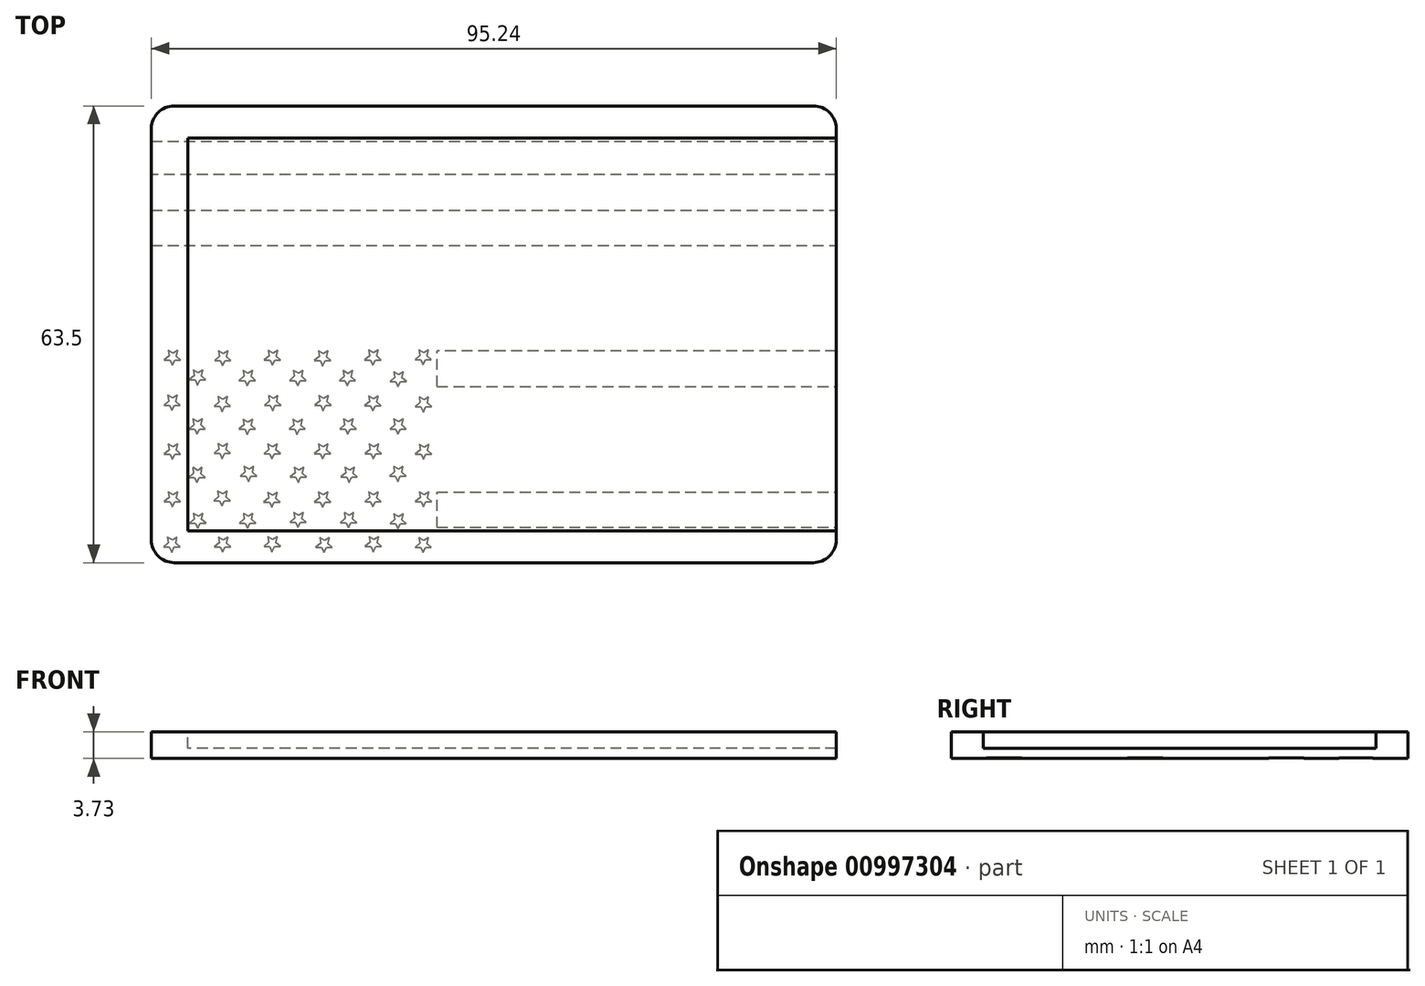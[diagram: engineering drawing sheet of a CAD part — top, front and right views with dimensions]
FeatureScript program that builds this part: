
annotation { "Feature Type Name" : "Feature", "Feature Type Description" : "" }
export const myFeature = defineFeature(function(context is Context, id is Id, definition is map)
    precondition{}
    {
        {
            var Q0;
            Q0=qCreatedBy(makeId("Top.planeOp"),FACE);
            var sketch = newSketch(context, id + "F0", { "sketchPlane" : qUnion([Q0])});
            skLineSegment(sketch, "E0.bottom", {"start": v(44.45, -31.75) * mm, "end": v(-44.45, -31.75) * mm});
            skLineSegment(sketch, "E0.top", {"start": v(44.45, 31.75) * mm, "end": v(-44.45, 31.75) * mm});
            skLineSegment(sketch, "E0.left", {"start": v(47.63, -28.57) * mm, "end": v(47.62, 28.58) * mm});
            skLineSegment(sketch, "E0.right", {"start": v(-47.63, -28.58) * mm, "end": v(-47.63, 28.57) * mm});
            skPoint(sketch, "E0.middle", {"position": v(0, 0) * mm});
            skPoint(sketch, "E1.visualSharp", {"position": v(47.62, 31.75) * mm});
            skArc(sketch, "E1.filletArc", {"start": v(47.62, 28.58) * mm, "mid": v(46.7, 30.82) * mm, "end": v(44.45, 31.75) * mm});
            skPoint(sketch, "E2.visualSharp", {"position": v(47.63, -31.75) * mm});
            skArc(sketch, "E2.filletArc", {"start": v(44.45, -31.75) * mm, "mid": v(46.7, -30.82) * mm, "end": v(47.62, -28.57) * mm});
            skPoint(sketch, "E3.visualSharp", {"position": v(-47.62, -31.75) * mm});
            skArc(sketch, "E3.filletArc", {"start": v(-47.62, -28.58) * mm, "mid": v(-46.7, -30.82) * mm, "end": v(-44.45, -31.75) * mm});
            skPoint(sketch, "E4.visualSharp", {"position": v(-47.63, 31.75) * mm});
            skArc(sketch, "E4.filletArc", {"start": v(-44.45, 31.75) * mm, "mid": v(-46.7, 30.82) * mm, "end": v(-47.63, 28.57) * mm});
            skSolve(sketch);
        }
        {
            var Q0;
            Q0=makeQuery(id+"F0.imprint","IMPRINT",FACE,{"disambiguationData":[TD([[makeQuery(id+"F0.imprint","IMPRINT",EDGE,{"derivedFrom":sQuery(id+"F0.wireOp",EDGE,"E0.bottom")}),-1.0]])]});
            extrude(context, id + "F1", {"entities" : qUnion([Q0]), "depth" : 3.73 * mm, "offsetDistance" : 25.4 * mm});
        }
        {
            var Q0;
            Q0=makeQuery(id+"F1.opExtrude","CAP_FACE",FACE,{"disambiguationData":[OSD([sQuery(id+"F0.wireOp",EDGE,"E0.bottom"),sQuery(id+"F0.wireOp",EDGE,"E0.top"),sQuery(id+"F0.wireOp",EDGE,"E0.left"),sQuery(id+"F0.wireOp",EDGE,"E0.right"),sQuery(id+"F0.wireOp",EDGE,"E1.filletArc"),sQuery(id+"F0.wireOp",EDGE,"E2.filletArc"),sQuery(id+"F0.wireOp",EDGE,"E3.filletArc"),sQuery(id+"F0.wireOp",EDGE,"E4.filletArc")])],"isStart":false});
            var sketch = newSketch(context, id + "F2", { "sketchPlane" : qUnion([Q0])});
            skLineSegment(sketch, "E5.bottom", {"start": v(47.62, 27.3) * mm, "end": v(-42.55, 27.3) * mm});
            skLineSegment(sketch, "E5.top", {"start": v(47.63, -27.3) * mm, "end": v(-42.55, -27.3) * mm});
            skLineSegment(sketch, "E5.left", {"start": v(47.62, 27.3) * mm, "end": v(47.62, -27.3) * mm});
            skLineSegment(sketch, "E5.right", {"start": v(-42.55, 27.3) * mm, "end": v(-42.55, -27.3) * mm});
            skSolve(sketch);
        }
        {
            var Q0;
            Q0=makeQuery(id+"F2.imprint","IMPRINT",FACE,{"disambiguationData":[TD([[makeQuery(id+"F2.imprint","IMPRINT",EDGE,{"derivedFrom":sQuery(id+"F2.wireOp",EDGE,"E5.bottom")}),1.0]])]});
            extrude(context, id + "F3", {"entities" : qUnion([Q0]), "operationType" : NewBodyOperationType.REMOVE, "oppositeDirection" : true, "depth" : 2.3 * mm, "offsetDistance" : 25.4 * mm});
        }
        {
            var Q0;
            Q0=makeQuery(id+"F1.opExtrude","CAP_FACE",FACE,{"disambiguationData":[OSD([sQuery(id+"F0.wireOp",EDGE,"E0.bottom"),sQuery(id+"F0.wireOp",EDGE,"E0.top"),sQuery(id+"F0.wireOp",EDGE,"E0.left"),sQuery(id+"F0.wireOp",EDGE,"E0.right"),sQuery(id+"F0.wireOp",EDGE,"E1.filletArc"),sQuery(id+"F0.wireOp",EDGE,"E2.filletArc"),sQuery(id+"F0.wireOp",EDGE,"E3.filletArc"),sQuery(id+"F0.wireOp",EDGE,"E4.filletArc")])],"isStart":true});
            var sketch = newSketch(context, id + "F4", { "sketchPlane" : qUnion([Q0])});
            skLineSegment(sketch, "E6.top", {"start": v(-8.6, 26.85) * mm, "end": v(47.63, 26.85) * mm});
            skLineSegment(sketch, "E6.left", {"start": v(-8.6, 31.75) * mm, "end": v(-8.6, 30.82) * mm});
            skLineSegment(sketch, "E7.top", {"start": v(-8.6, 21.95) * mm, "end": v(47.63, 21.95) * mm});
            skLineSegment(sketch, "E7.right", {"start": v(47.63, 26.85) * mm, "end": v(47.63, 21.95) * mm});
            skLineSegment(sketch, "E8.top", {"start": v(-8.6, 17.04) * mm, "end": v(47.63, 17.04) * mm});
            skLineSegment(sketch, "E8.right", {"start": v(47.63, 21.95) * mm, "end": v(47.63, 17.04) * mm});
            skLineSegment(sketch, "E9.right", {"start": v(47.63, 17.04) * mm, "end": v(47.63, 7.24) * mm});
            skLineSegment(sketch, "E10.bottom", {"start": v(47.63, 17.04) * mm, "end": v(-8.6, 17.04) * mm});
            skLineSegment(sketch, "E10.top", {"start": v(47.62, 12.14) * mm, "end": v(-8.16, 12.14) * mm});
            skLineSegment(sketch, "E10.left", {"start": v(47.63, 17.04) * mm, "end": v(47.63, 12.14) * mm});
            skLineSegment(sketch, "E11.left", {"start": v(47.63, 12.14) * mm, "end": v(47.63, 7.24) * mm});
            skLineSegment(sketch, "E12.bottom", {"start": v(-46.7, 7.24) * mm, "end": v(-47.63, 7.24) * mm});
            skPoint(sketch, "E13.orphan", {"position": v(47.63, 0) * mm});
            skLineSegment(sketch, "E14.bottom", {"start": v(-47.63, 7.24) * mm, "end": v(-46.7, 7.24) * mm});
            skLineSegment(sketch, "E14.right", {"start": v(47.63, 7.24) * mm, "end": v(47.63, 0) * mm});
            skLineSegment(sketch, "E15.top", {"start": v(47.62, 2.34) * mm, "end": v(-7.88, 2.34) * mm});
            skLineSegment(sketch, "E15.left", {"start": v(47.63, 2.34) * mm, "end": v(47.63, 0) * mm});
            skLineSegment(sketch, "E16.bottom", {"start": v(-47.62, 2.34) * mm, "end": v(-46.7, 2.34) * mm});
            skLineSegment(sketch, "E16.top", {"start": v(-47.63, -2.57) * mm, "end": v(47.63, -2.57) * mm});
            skLineSegment(sketch, "E16.left", {"start": v(-47.63, 2.34) * mm, "end": v(-47.63, -2.57) * mm});
            skLineSegment(sketch, "E16.right", {"start": v(47.62, 2.34) * mm, "end": v(47.62, -2.57) * mm});
            skLineSegment(sketch, "E17.bottom", {"start": v(47.63, -2.57) * mm, "end": v(-47.63, -2.57) * mm});
            skLineSegment(sketch, "E17.left", {"start": v(47.62, -2.57) * mm, "end": v(47.62, -7.47) * mm});
            skLineSegment(sketch, "E17.right", {"start": v(-47.63, -2.57) * mm, "end": v(-47.63, -7.47) * mm});
            skLineSegment(sketch, "E18.bottom", {"start": v(47.62, -7.47) * mm, "end": v(-47.63, -7.47) * mm});
            skPoint(sketch, "E19.orphan", {"position": v(-7.88, 0) * mm});
            skLineSegment(sketch, "E20.bottom", {"start": v(-47.63, -7.47) * mm, "end": v(47.62, -7.47) * mm});
            skLineSegment(sketch, "E20.top", {"start": v(-47.63, -12.37) * mm, "end": v(47.62, -12.37) * mm});
            skLineSegment(sketch, "E20.left", {"start": v(-47.63, -7.47) * mm, "end": v(-47.63, -12.37) * mm});
            skLineSegment(sketch, "E20.right", {"start": v(47.62, -7.47) * mm, "end": v(47.62, -12.37) * mm});
            skLineSegment(sketch, "E21.top", {"start": v(-47.63, -17.27) * mm, "end": v(47.62, -17.27) * mm});
            skLineSegment(sketch, "E21.left", {"start": v(-47.63, -12.37) * mm, "end": v(-47.63, -17.27) * mm});
            skLineSegment(sketch, "E21.right", {"start": v(47.62, -12.37) * mm, "end": v(47.62, -17.27) * mm});
            skLineSegment(sketch, "E22.bottom", {"start": v(47.62, -17.27) * mm, "end": v(-47.63, -17.27) * mm});
            skLineSegment(sketch, "E22.top", {"start": v(47.62, -22.17) * mm, "end": v(-47.63, -22.17) * mm});
            skLineSegment(sketch, "E22.left", {"start": v(47.62, -17.27) * mm, "end": v(47.62, -22.17) * mm});
            skLineSegment(sketch, "E22.right", {"start": v(-47.63, -17.27) * mm, "end": v(-47.63, -22.17) * mm});
            skLineSegment(sketch, "E23", {"start": v(-47.63, -26.85) * mm, "end": v(47.62, -26.85) * mm});
            skLineSegment(sketch, "E24.trimOffspring", {"start": v(-8.05, 7.24) * mm, "end": v(47.63, 7.24) * mm});
            skPoint(sketch, "E25.left.start.orphan", {"position": v(-46.7, 30.82) * mm});
            skLineSegment(sketch, "E26.bottom", {"start": v(-8.6, 30.82) * mm, "end": v(-7.88, 30.82) * mm});
            skLineSegment(sketch, "E26.right", {"start": v(-7.88, 30.82) * mm, "end": v(-7.88, 2.34) * mm});
            skLineSegment(sketch, "E27.trimOffspring", {"start": v(-7.88, 2.34) * mm, "end": v(47.62, 2.34) * mm});
            skPoint(sketch, "E25.right.start.orphan", {"position": v(-8.6, 30.82) * mm});
            skLineSegment(sketch, "E28", {"start": v(-45.92, 29.59) * mm, "end": v(-45.14, 29.59) * mm});
            skLineSegment(sketch, "E29", {"start": v(-45.14, 29.59) * mm, "end": v(-44.8, 30.3) * mm});
            skLineSegment(sketch, "E30", {"start": v(-44.8, 30.3) * mm, "end": v(-44.44, 29.59) * mm});
            skLineSegment(sketch, "E31", {"start": v(-44.44, 29.59) * mm, "end": v(-43.65, 29.59) * mm});
            skLineSegment(sketch, "E32", {"start": v(-43.65, 29.59) * mm, "end": v(-44.23, 29.06) * mm});
            skLineSegment(sketch, "E33", {"start": v(-44.23, 29.06) * mm, "end": v(-44.06, 28.23) * mm});
            skLineSegment(sketch, "E34", {"start": v(-44.06, 28.23) * mm, "end": v(-44.67, 28.61) * mm});
            skLineSegment(sketch, "E35", {"start": v(-44.67, 28.61) * mm, "end": v(-45.38, 28.23) * mm});
            skLineSegment(sketch, "E36", {"start": v(-45.38, 28.23) * mm, "end": v(-45.26, 29.01) * mm});
            skLineSegment(sketch, "E37", {"start": v(-45.26, 29.01) * mm, "end": v(-45.92, 29.59) * mm});
            skLineSegment(sketch, "E38", {"start": v(-38.84, 29.57) * mm, "end": v(-38.05, 29.57) * mm});
            skLineSegment(sketch, "E39", {"start": v(-38.05, 29.57) * mm, "end": v(-37.71, 30.28) * mm});
            skLineSegment(sketch, "E40", {"start": v(-37.71, 30.28) * mm, "end": v(-37.36, 29.57) * mm});
            skLineSegment(sketch, "E41", {"start": v(-37.36, 29.57) * mm, "end": v(-36.57, 29.57) * mm});
            skLineSegment(sketch, "E42", {"start": v(-36.57, 29.57) * mm, "end": v(-37.14, 29.04) * mm});
            skLineSegment(sketch, "E43", {"start": v(-37.14, 29.04) * mm, "end": v(-36.97, 28.2) * mm});
            skLineSegment(sketch, "E44", {"start": v(-36.97, 28.2) * mm, "end": v(-37.59, 28.6) * mm});
            skLineSegment(sketch, "E45", {"start": v(-37.59, 28.6) * mm, "end": v(-38.3, 28.2) * mm});
            skLineSegment(sketch, "E46", {"start": v(-38.3, 28.2) * mm, "end": v(-38.18, 29) * mm});
            skLineSegment(sketch, "E47", {"start": v(-38.18, 29) * mm, "end": v(-38.84, 29.57) * mm});
            skLineSegment(sketch, "E48", {"start": v(-21.49, 6.44) * mm, "end": v(-20.7, 6.44) * mm});
            skLineSegment(sketch, "E49", {"start": v(-20.7, 6.44) * mm, "end": v(-20.36, 7.15) * mm});
            skLineSegment(sketch, "E50", {"start": v(-20.36, 7.15) * mm, "end": v(-20, 6.44) * mm});
            skLineSegment(sketch, "E51", {"start": v(-20, 6.44) * mm, "end": v(-19.22, 6.44) * mm});
            skLineSegment(sketch, "E52", {"start": v(-19.22, 6.44) * mm, "end": v(-19.8, 5.91) * mm});
            skLineSegment(sketch, "E53", {"start": v(-19.8, 5.91) * mm, "end": v(-19.62, 5.08) * mm});
            skLineSegment(sketch, "E54", {"start": v(-19.62, 5.08) * mm, "end": v(-20.23, 5.47) * mm});
            skLineSegment(sketch, "E55", {"start": v(-20.23, 5.47) * mm, "end": v(-20.94, 5.08) * mm});
            skLineSegment(sketch, "E56", {"start": v(-20.94, 5.08) * mm, "end": v(-20.82, 5.86) * mm});
            skLineSegment(sketch, "E57", {"start": v(-20.82, 5.86) * mm, "end": v(-21.49, 6.44) * mm});
            skLineSegment(sketch, "E58", {"start": v(-17.94, 3.57) * mm, "end": v(-17.16, 3.57) * mm});
            skLineSegment(sketch, "E59", {"start": v(-17.16, 3.57) * mm, "end": v(-16.82, 4.29) * mm});
            skLineSegment(sketch, "E60", {"start": v(-16.82, 4.29) * mm, "end": v(-16.46, 3.57) * mm});
            skLineSegment(sketch, "E61", {"start": v(-16.46, 3.57) * mm, "end": v(-15.67, 3.57) * mm});
            skLineSegment(sketch, "E62", {"start": v(-15.67, 3.57) * mm, "end": v(-16.25, 3.05) * mm});
            skLineSegment(sketch, "E63", {"start": v(-16.25, 3.05) * mm, "end": v(-16.07, 2.21) * mm});
            skLineSegment(sketch, "E64", {"start": v(-16.07, 2.21) * mm, "end": v(-16.69, 2.6) * mm});
            skLineSegment(sketch, "E65", {"start": v(-16.69, 2.6) * mm, "end": v(-17.4, 2.21) * mm});
            skLineSegment(sketch, "E66", {"start": v(-17.4, 2.21) * mm, "end": v(-17.28, 3) * mm});
            skLineSegment(sketch, "E67", {"start": v(-17.28, 3) * mm, "end": v(-17.94, 3.57) * mm});
            skLineSegment(sketch, "E68", {"start": v(-14.43, 6.57) * mm, "end": v(-13.65, 6.57) * mm});
            skLineSegment(sketch, "E69", {"start": v(-13.65, 6.57) * mm, "end": v(-13.3, 7.29) * mm});
            skLineSegment(sketch, "E70", {"start": v(-13.3, 7.29) * mm, "end": v(-12.95, 6.57) * mm});
            skLineSegment(sketch, "E71", {"start": v(-12.95, 6.57) * mm, "end": v(-12.16, 6.57) * mm});
            skLineSegment(sketch, "E72", {"start": v(-12.16, 6.57) * mm, "end": v(-12.74, 6.05) * mm});
            skLineSegment(sketch, "E73", {"start": v(-12.74, 6.05) * mm, "end": v(-12.56, 5.21) * mm});
            skLineSegment(sketch, "E74", {"start": v(-12.56, 5.21) * mm, "end": v(-13.18, 5.6) * mm});
            skLineSegment(sketch, "E75", {"start": v(-13.18, 5.6) * mm, "end": v(-13.9, 5.21) * mm});
            skLineSegment(sketch, "E76", {"start": v(-13.9, 5.21) * mm, "end": v(-13.77, 6) * mm});
            skLineSegment(sketch, "E77", {"start": v(-13.77, 6) * mm, "end": v(-14.43, 6.57) * mm});
            skLineSegment(sketch, "E78", {"start": v(-10.94, 3.53) * mm, "end": v(-10.16, 3.53) * mm});
            skLineSegment(sketch, "E79", {"start": v(-10.16, 3.53) * mm, "end": v(-9.82, 4.25) * mm});
            skLineSegment(sketch, "E80", {"start": v(-9.82, 4.25) * mm, "end": v(-9.46, 3.53) * mm});
            skLineSegment(sketch, "E81", {"start": v(-9.46, 3.53) * mm, "end": v(-8.67, 3.53) * mm});
            skLineSegment(sketch, "E82", {"start": v(-8.67, 3.53) * mm, "end": v(-9.25, 3) * mm});
            skLineSegment(sketch, "E83", {"start": v(-9.25, 3) * mm, "end": v(-9.08, 2.17) * mm});
            skLineSegment(sketch, "E84", {"start": v(-9.08, 2.17) * mm, "end": v(-9.7, 2.56) * mm});
            skLineSegment(sketch, "E85", {"start": v(-9.7, 2.56) * mm, "end": v(-10.4, 2.17) * mm});
            skLineSegment(sketch, "E86", {"start": v(-10.4, 2.17) * mm, "end": v(-10.28, 2.96) * mm});
            skLineSegment(sketch, "E87", {"start": v(-10.28, 2.96) * mm, "end": v(-10.94, 3.53) * mm});
            skLineSegment(sketch, "E88", {"start": v(-10.92, 10.08) * mm, "end": v(-10.14, 10.08) * mm});
            skLineSegment(sketch, "E89", {"start": v(-10.14, 10.08) * mm, "end": v(-9.8, 10.8) * mm});
            skLineSegment(sketch, "E90", {"start": v(-9.8, 10.8) * mm, "end": v(-9.44, 10.08) * mm});
            skLineSegment(sketch, "E91", {"start": v(-9.44, 10.08) * mm, "end": v(-8.65, 10.08) * mm});
            skLineSegment(sketch, "E92", {"start": v(-8.65, 10.08) * mm, "end": v(-9.23, 9.56) * mm});
            skLineSegment(sketch, "E93", {"start": v(-9.23, 9.56) * mm, "end": v(-9.06, 8.72) * mm});
            skLineSegment(sketch, "E94", {"start": v(-9.06, 8.72) * mm, "end": v(-9.67, 9.1) * mm});
            skLineSegment(sketch, "E95", {"start": v(-9.67, 9.1) * mm, "end": v(-10.38, 8.72) * mm});
            skLineSegment(sketch, "E96", {"start": v(-10.38, 8.72) * mm, "end": v(-10.26, 9.5) * mm});
            skLineSegment(sketch, "E97", {"start": v(-10.26, 9.5) * mm, "end": v(-10.92, 10.08) * mm});
            skLineSegment(sketch, "E98", {"start": v(-17.96, 9.95) * mm, "end": v(-17.17, 9.95) * mm});
            skLineSegment(sketch, "E99", {"start": v(-17.17, 9.95) * mm, "end": v(-16.83, 10.66) * mm});
            skLineSegment(sketch, "E100", {"start": v(-16.83, 10.66) * mm, "end": v(-16.48, 9.95) * mm});
            skLineSegment(sketch, "E101", {"start": v(-16.48, 9.95) * mm, "end": v(-15.69, 9.95) * mm});
            skLineSegment(sketch, "E102", {"start": v(-15.69, 9.95) * mm, "end": v(-16.26, 9.42) * mm});
            skLineSegment(sketch, "E103", {"start": v(-16.26, 9.42) * mm, "end": v(-16.1, 8.59) * mm});
            skLineSegment(sketch, "E104", {"start": v(-16.1, 8.59) * mm, "end": v(-16.7, 8.97) * mm});
            skLineSegment(sketch, "E105", {"start": v(-16.7, 8.97) * mm, "end": v(-17.42, 8.59) * mm});
            skLineSegment(sketch, "E106", {"start": v(-17.42, 8.59) * mm, "end": v(-17.3, 9.37) * mm});
            skLineSegment(sketch, "E107", {"start": v(-17.3, 9.37) * mm, "end": v(-17.96, 9.95) * mm});
            skLineSegment(sketch, "E108", {"start": v(-24.93, 3.67) * mm, "end": v(-24.15, 3.67) * mm});
            skLineSegment(sketch, "E109", {"start": v(-24.15, 3.67) * mm, "end": v(-23.81, 4.38) * mm});
            skLineSegment(sketch, "E110", {"start": v(-23.81, 4.38) * mm, "end": v(-23.45, 3.67) * mm});
            skLineSegment(sketch, "E111", {"start": v(-23.45, 3.67) * mm, "end": v(-22.66, 3.67) * mm});
            skLineSegment(sketch, "E112", {"start": v(-22.66, 3.67) * mm, "end": v(-23.24, 3.14) * mm});
            skLineSegment(sketch, "E113", {"start": v(-23.24, 3.14) * mm, "end": v(-23.07, 2.3) * mm});
            skLineSegment(sketch, "E114", {"start": v(-23.07, 2.3) * mm, "end": v(-23.68, 2.7) * mm});
            skLineSegment(sketch, "E115", {"start": v(-23.68, 2.7) * mm, "end": v(-24.4, 2.3) * mm});
            skLineSegment(sketch, "E116", {"start": v(-24.4, 2.3) * mm, "end": v(-24.27, 3.1) * mm});
            skLineSegment(sketch, "E117", {"start": v(-24.27, 3.1) * mm, "end": v(-24.93, 3.67) * mm});
            skLineSegment(sketch, "E118", {"start": v(-42.3, 26.26) * mm, "end": v(-41.52, 26.26) * mm});
            skLineSegment(sketch, "E119", {"start": v(-41.52, 26.26) * mm, "end": v(-41.18, 26.97) * mm});
            skLineSegment(sketch, "E120", {"start": v(-41.18, 26.97) * mm, "end": v(-40.82, 26.26) * mm});
            skLineSegment(sketch, "E121", {"start": v(-40.82, 26.26) * mm, "end": v(-40.04, 26.26) * mm});
            skLineSegment(sketch, "E122", {"start": v(-40.04, 26.26) * mm, "end": v(-40.61, 25.73) * mm});
            skLineSegment(sketch, "E123", {"start": v(-40.61, 25.73) * mm, "end": v(-40.44, 24.9) * mm});
            skLineSegment(sketch, "E124", {"start": v(-40.44, 24.9) * mm, "end": v(-41.05, 25.28) * mm});
            skLineSegment(sketch, "E125", {"start": v(-41.05, 25.28) * mm, "end": v(-41.76, 24.9) * mm});
            skLineSegment(sketch, "E126", {"start": v(-41.76, 24.9) * mm, "end": v(-41.64, 25.68) * mm});
            skLineSegment(sketch, "E127", {"start": v(-41.64, 25.68) * mm, "end": v(-42.3, 26.26) * mm});
            skLineSegment(sketch, "E128", {"start": v(-45.83, 23.27) * mm, "end": v(-45.05, 23.27) * mm});
            skLineSegment(sketch, "E129", {"start": v(-45.05, 23.27) * mm, "end": v(-44.7, 23.99) * mm});
            skLineSegment(sketch, "E130", {"start": v(-44.7, 23.99) * mm, "end": v(-44.35, 23.27) * mm});
            skLineSegment(sketch, "E131", {"start": v(-44.35, 23.27) * mm, "end": v(-43.56, 23.27) * mm});
            skLineSegment(sketch, "E132", {"start": v(-43.56, 23.27) * mm, "end": v(-44.14, 22.75) * mm});
            skLineSegment(sketch, "E133", {"start": v(-44.14, 22.75) * mm, "end": v(-43.97, 21.91) * mm});
            skLineSegment(sketch, "E134", {"start": v(-43.97, 21.91) * mm, "end": v(-44.58, 22.3) * mm});
            skLineSegment(sketch, "E135", {"start": v(-44.58, 22.3) * mm, "end": v(-45.3, 21.91) * mm});
            skLineSegment(sketch, "E136", {"start": v(-45.3, 21.91) * mm, "end": v(-45.17, 22.7) * mm});
            skLineSegment(sketch, "E137", {"start": v(-45.17, 22.7) * mm, "end": v(-45.83, 23.27) * mm});
            skLineSegment(sketch, "E138", {"start": v(-38.93, 23.16) * mm, "end": v(-38.15, 23.16) * mm});
            skLineSegment(sketch, "E139", {"start": v(-38.15, 23.16) * mm, "end": v(-37.8, 23.87) * mm});
            skLineSegment(sketch, "E140", {"start": v(-37.8, 23.87) * mm, "end": v(-37.45, 23.16) * mm});
            skLineSegment(sketch, "E141", {"start": v(-37.45, 23.16) * mm, "end": v(-36.66, 23.16) * mm});
            skLineSegment(sketch, "E142", {"start": v(-36.66, 23.16) * mm, "end": v(-37.24, 22.63) * mm});
            skLineSegment(sketch, "E143", {"start": v(-37.24, 22.63) * mm, "end": v(-37.07, 21.8) * mm});
            skLineSegment(sketch, "E144", {"start": v(-37.07, 21.8) * mm, "end": v(-37.68, 22.18) * mm});
            skLineSegment(sketch, "E145", {"start": v(-37.68, 22.18) * mm, "end": v(-38.4, 21.8) * mm});
            skLineSegment(sketch, "E146", {"start": v(-38.4, 21.8) * mm, "end": v(-38.27, 22.58) * mm});
            skLineSegment(sketch, "E147", {"start": v(-38.27, 22.58) * mm, "end": v(-38.93, 23.16) * mm});
            skLineSegment(sketch, "E148", {"start": v(-35.37, 26.26) * mm, "end": v(-34.58, 26.26) * mm});
            skLineSegment(sketch, "E149", {"start": v(-34.58, 26.26) * mm, "end": v(-34.24, 26.97) * mm});
            skLineSegment(sketch, "E150", {"start": v(-34.24, 26.97) * mm, "end": v(-33.89, 26.26) * mm});
            skLineSegment(sketch, "E151", {"start": v(-33.89, 26.26) * mm, "end": v(-33.1, 26.26) * mm});
            skLineSegment(sketch, "E152", {"start": v(-33.1, 26.26) * mm, "end": v(-33.67, 25.73) * mm});
            skLineSegment(sketch, "E153", {"start": v(-33.67, 25.73) * mm, "end": v(-33.5, 24.9) * mm});
            skLineSegment(sketch, "E154", {"start": v(-33.5, 24.9) * mm, "end": v(-34.12, 25.28) * mm});
            skLineSegment(sketch, "E155", {"start": v(-34.12, 25.28) * mm, "end": v(-34.83, 24.9) * mm});
            skLineSegment(sketch, "E156", {"start": v(-34.83, 24.9) * mm, "end": v(-34.7, 25.68) * mm});
            skLineSegment(sketch, "E157", {"start": v(-34.7, 25.68) * mm, "end": v(-35.37, 26.26) * mm});
            skLineSegment(sketch, "E158", {"start": v(-31.96, 29.51) * mm, "end": v(-31.17, 29.51) * mm});
            skLineSegment(sketch, "E159", {"start": v(-31.17, 29.51) * mm, "end": v(-30.83, 30.23) * mm});
            skLineSegment(sketch, "E160", {"start": v(-30.83, 30.23) * mm, "end": v(-30.48, 29.51) * mm});
            skLineSegment(sketch, "E161", {"start": v(-30.48, 29.51) * mm, "end": v(-29.69, 29.51) * mm});
            skLineSegment(sketch, "E162", {"start": v(-29.69, 29.51) * mm, "end": v(-30.26, 28.99) * mm});
            skLineSegment(sketch, "E163", {"start": v(-30.26, 28.99) * mm, "end": v(-30.1, 28.15) * mm});
            skLineSegment(sketch, "E164", {"start": v(-30.1, 28.15) * mm, "end": v(-30.7, 28.54) * mm});
            skLineSegment(sketch, "E165", {"start": v(-30.7, 28.54) * mm, "end": v(-31.42, 28.15) * mm});
            skLineSegment(sketch, "E166", {"start": v(-31.42, 28.15) * mm, "end": v(-31.3, 28.94) * mm});
            skLineSegment(sketch, "E167", {"start": v(-31.3, 28.94) * mm, "end": v(-31.96, 29.51) * mm});
            skLineSegment(sketch, "E168", {"start": v(-28.35, 26.14) * mm, "end": v(-27.57, 26.14) * mm});
            skLineSegment(sketch, "E169", {"start": v(-27.57, 26.14) * mm, "end": v(-27.23, 26.86) * mm});
            skLineSegment(sketch, "E170", {"start": v(-27.23, 26.86) * mm, "end": v(-26.87, 26.14) * mm});
            skLineSegment(sketch, "E171", {"start": v(-26.87, 26.14) * mm, "end": v(-26.08, 26.14) * mm});
            skLineSegment(sketch, "E172", {"start": v(-26.08, 26.14) * mm, "end": v(-26.66, 25.62) * mm});
            skLineSegment(sketch, "E173", {"start": v(-26.66, 25.62) * mm, "end": v(-26.49, 24.78) * mm});
            skLineSegment(sketch, "E174", {"start": v(-26.49, 24.78) * mm, "end": v(-27.1, 25.17) * mm});
            skLineSegment(sketch, "E175", {"start": v(-27.1, 25.17) * mm, "end": v(-27.81, 24.78) * mm});
            skLineSegment(sketch, "E176", {"start": v(-27.81, 24.78) * mm, "end": v(-27.7, 25.56) * mm});
            skLineSegment(sketch, "E177", {"start": v(-27.7, 25.56) * mm, "end": v(-28.35, 26.14) * mm});
            skLineSegment(sketch, "E178", {"start": v(-24.75, 29.63) * mm, "end": v(-23.97, 29.63) * mm});
            skLineSegment(sketch, "E179", {"start": v(-23.97, 29.63) * mm, "end": v(-23.63, 30.34) * mm});
            skLineSegment(sketch, "E180", {"start": v(-23.63, 30.34) * mm, "end": v(-23.27, 29.63) * mm});
            skLineSegment(sketch, "E181", {"start": v(-23.27, 29.63) * mm, "end": v(-22.48, 29.63) * mm});
            skLineSegment(sketch, "E182", {"start": v(-22.48, 29.63) * mm, "end": v(-23.05, 29.1) * mm});
            skLineSegment(sketch, "E183", {"start": v(-23.05, 29.1) * mm, "end": v(-22.88, 28.27) * mm});
            skLineSegment(sketch, "E184", {"start": v(-22.88, 28.27) * mm, "end": v(-23.5, 28.66) * mm});
            skLineSegment(sketch, "E185", {"start": v(-23.5, 28.66) * mm, "end": v(-24.2, 28.27) * mm});
            skLineSegment(sketch, "E186", {"start": v(-24.2, 28.27) * mm, "end": v(-24.09, 29.05) * mm});
            skLineSegment(sketch, "E187", {"start": v(-24.09, 29.05) * mm, "end": v(-24.75, 29.63) * mm});
            skLineSegment(sketch, "E188", {"start": v(-21.34, 26.18) * mm, "end": v(-20.55, 26.18) * mm});
            skLineSegment(sketch, "E189", {"start": v(-20.55, 26.18) * mm, "end": v(-20.21, 26.9) * mm});
            skLineSegment(sketch, "E190", {"start": v(-20.21, 26.9) * mm, "end": v(-19.86, 26.18) * mm});
            skLineSegment(sketch, "E191", {"start": v(-19.86, 26.18) * mm, "end": v(-19.07, 26.18) * mm});
            skLineSegment(sketch, "E192", {"start": v(-19.07, 26.18) * mm, "end": v(-19.64, 25.66) * mm});
            skLineSegment(sketch, "E193", {"start": v(-19.64, 25.66) * mm, "end": v(-19.47, 24.82) * mm});
            skLineSegment(sketch, "E194", {"start": v(-19.47, 24.82) * mm, "end": v(-20.09, 25.2) * mm});
            skLineSegment(sketch, "E195", {"start": v(-20.09, 25.2) * mm, "end": v(-20.8, 24.82) * mm});
            skLineSegment(sketch, "E196", {"start": v(-20.8, 24.82) * mm, "end": v(-20.68, 25.6) * mm});
            skLineSegment(sketch, "E197", {"start": v(-20.68, 25.6) * mm, "end": v(-21.34, 26.18) * mm});
            skLineSegment(sketch, "E198", {"start": v(-17.89, 29.51) * mm, "end": v(-17.1, 29.51) * mm});
            skLineSegment(sketch, "E199", {"start": v(-17.1, 29.51) * mm, "end": v(-16.77, 30.23) * mm});
            skLineSegment(sketch, "E200", {"start": v(-16.77, 30.23) * mm, "end": v(-16.4, 29.51) * mm});
            skLineSegment(sketch, "E201", {"start": v(-16.4, 29.51) * mm, "end": v(-15.62, 29.51) * mm});
            skLineSegment(sketch, "E202", {"start": v(-15.62, 29.51) * mm, "end": v(-16.2, 28.99) * mm});
            skLineSegment(sketch, "E203", {"start": v(-16.2, 28.99) * mm, "end": v(-16.02, 28.15) * mm});
            skLineSegment(sketch, "E204", {"start": v(-16.02, 28.15) * mm, "end": v(-16.64, 28.54) * mm});
            skLineSegment(sketch, "E205", {"start": v(-16.64, 28.54) * mm, "end": v(-17.35, 28.15) * mm});
            skLineSegment(sketch, "E206", {"start": v(-17.35, 28.15) * mm, "end": v(-17.23, 28.94) * mm});
            skLineSegment(sketch, "E207", {"start": v(-17.23, 28.94) * mm, "end": v(-17.89, 29.51) * mm});
            skLineSegment(sketch, "E208", {"start": v(-14.44, 26.33) * mm, "end": v(-13.66, 26.33) * mm});
            skLineSegment(sketch, "E209", {"start": v(-13.66, 26.33) * mm, "end": v(-13.32, 27.05) * mm});
            skLineSegment(sketch, "E210", {"start": v(-13.32, 27.05) * mm, "end": v(-12.96, 26.33) * mm});
            skLineSegment(sketch, "E211", {"start": v(-12.96, 26.33) * mm, "end": v(-12.17, 26.33) * mm});
            skLineSegment(sketch, "E212", {"start": v(-12.17, 26.33) * mm, "end": v(-12.75, 25.81) * mm});
            skLineSegment(sketch, "E213", {"start": v(-12.75, 25.81) * mm, "end": v(-12.57, 24.98) * mm});
            skLineSegment(sketch, "E214", {"start": v(-12.57, 24.98) * mm, "end": v(-13.19, 25.36) * mm});
            skLineSegment(sketch, "E215", {"start": v(-13.19, 25.36) * mm, "end": v(-13.9, 24.98) * mm});
            skLineSegment(sketch, "E216", {"start": v(-13.9, 24.98) * mm, "end": v(-13.78, 25.76) * mm});
            skLineSegment(sketch, "E217", {"start": v(-13.78, 25.76) * mm, "end": v(-14.44, 26.33) * mm});
            skLineSegment(sketch, "E218", {"start": v(-10.95, 29.63) * mm, "end": v(-10.17, 29.63) * mm});
            skLineSegment(sketch, "E219", {"start": v(-10.17, 29.63) * mm, "end": v(-9.83, 30.34) * mm});
            skLineSegment(sketch, "E220", {"start": v(-9.83, 30.34) * mm, "end": v(-9.47, 29.63) * mm});
            skLineSegment(sketch, "E221", {"start": v(-9.47, 29.63) * mm, "end": v(-8.68, 29.63) * mm});
            skLineSegment(sketch, "E222", {"start": v(-8.68, 29.63) * mm, "end": v(-9.26, 29.1) * mm});
            skLineSegment(sketch, "E223", {"start": v(-9.26, 29.1) * mm, "end": v(-9.09, 28.27) * mm});
            skLineSegment(sketch, "E224", {"start": v(-9.09, 28.27) * mm, "end": v(-9.7, 28.66) * mm});
            skLineSegment(sketch, "E225", {"start": v(-9.7, 28.66) * mm, "end": v(-10.41, 28.27) * mm});
            skLineSegment(sketch, "E226", {"start": v(-10.41, 28.27) * mm, "end": v(-10.29, 29.05) * mm});
            skLineSegment(sketch, "E227", {"start": v(-10.29, 29.05) * mm, "end": v(-10.95, 29.63) * mm});
            skLineSegment(sketch, "E228", {"start": v(-10.91, 23.27) * mm, "end": v(-10.13, 23.27) * mm});
            skLineSegment(sketch, "E229", {"start": v(-10.13, 23.27) * mm, "end": v(-9.79, 23.99) * mm});
            skLineSegment(sketch, "E230", {"start": v(-9.79, 23.99) * mm, "end": v(-9.43, 23.27) * mm});
            skLineSegment(sketch, "E231", {"start": v(-9.43, 23.27) * mm, "end": v(-8.64, 23.27) * mm});
            skLineSegment(sketch, "E232", {"start": v(-8.64, 23.27) * mm, "end": v(-9.22, 22.75) * mm});
            skLineSegment(sketch, "E233", {"start": v(-9.22, 22.75) * mm, "end": v(-9.05, 21.91) * mm});
            skLineSegment(sketch, "E234", {"start": v(-9.05, 21.91) * mm, "end": v(-9.66, 22.3) * mm});
            skLineSegment(sketch, "E235", {"start": v(-9.66, 22.3) * mm, "end": v(-10.37, 21.91) * mm});
            skLineSegment(sketch, "E236", {"start": v(-10.37, 21.91) * mm, "end": v(-10.25, 22.7) * mm});
            skLineSegment(sketch, "E237", {"start": v(-10.25, 22.7) * mm, "end": v(-10.91, 23.27) * mm});
            skLineSegment(sketch, "E238", {"start": v(-17.93, 23.27) * mm, "end": v(-17.14, 23.27) * mm});
            skLineSegment(sketch, "E239", {"start": v(-17.14, 23.27) * mm, "end": v(-16.8, 23.99) * mm});
            skLineSegment(sketch, "E240", {"start": v(-16.8, 23.99) * mm, "end": v(-16.45, 23.27) * mm});
            skLineSegment(sketch, "E241", {"start": v(-16.45, 23.27) * mm, "end": v(-15.66, 23.27) * mm});
            skLineSegment(sketch, "E242", {"start": v(-15.66, 23.27) * mm, "end": v(-16.23, 22.75) * mm});
            skLineSegment(sketch, "E243", {"start": v(-16.23, 22.75) * mm, "end": v(-16.06, 21.91) * mm});
            skLineSegment(sketch, "E244", {"start": v(-16.06, 21.91) * mm, "end": v(-16.68, 22.3) * mm});
            skLineSegment(sketch, "E245", {"start": v(-16.68, 22.3) * mm, "end": v(-17.39, 21.91) * mm});
            skLineSegment(sketch, "E246", {"start": v(-17.39, 21.91) * mm, "end": v(-17.27, 22.7) * mm});
            skLineSegment(sketch, "E247", {"start": v(-17.27, 22.7) * mm, "end": v(-17.93, 23.27) * mm});
            skLineSegment(sketch, "E248", {"start": v(-24.94, 23.31) * mm, "end": v(-24.16, 23.31) * mm});
            skLineSegment(sketch, "E249", {"start": v(-24.16, 23.31) * mm, "end": v(-23.82, 24.03) * mm});
            skLineSegment(sketch, "E250", {"start": v(-23.82, 24.03) * mm, "end": v(-23.46, 23.31) * mm});
            skLineSegment(sketch, "E251", {"start": v(-23.46, 23.31) * mm, "end": v(-22.67, 23.31) * mm});
            skLineSegment(sketch, "E252", {"start": v(-22.67, 23.31) * mm, "end": v(-23.25, 22.79) * mm});
            skLineSegment(sketch, "E253", {"start": v(-23.25, 22.79) * mm, "end": v(-23.08, 21.95) * mm});
            skLineSegment(sketch, "E254", {"start": v(-23.08, 21.95) * mm, "end": v(-23.7, 22.34) * mm});
            skLineSegment(sketch, "E255", {"start": v(-23.7, 22.34) * mm, "end": v(-24.4, 21.95) * mm});
            skLineSegment(sketch, "E256", {"start": v(-24.4, 21.95) * mm, "end": v(-24.28, 22.74) * mm});
            skLineSegment(sketch, "E257", {"start": v(-24.28, 22.74) * mm, "end": v(-24.94, 23.31) * mm});
            skLineSegment(sketch, "E258", {"start": v(-32, 23.35) * mm, "end": v(-31.21, 23.35) * mm});
            skLineSegment(sketch, "E259", {"start": v(-31.21, 23.35) * mm, "end": v(-30.87, 24.06) * mm});
            skLineSegment(sketch, "E260", {"start": v(-30.87, 24.06) * mm, "end": v(-30.52, 23.35) * mm});
            skLineSegment(sketch, "E261", {"start": v(-30.52, 23.35) * mm, "end": v(-29.73, 23.35) * mm});
            skLineSegment(sketch, "E262", {"start": v(-29.73, 23.35) * mm, "end": v(-30.3, 22.83) * mm});
            skLineSegment(sketch, "E263", {"start": v(-30.3, 22.83) * mm, "end": v(-30.13, 22) * mm});
            skLineSegment(sketch, "E264", {"start": v(-30.13, 22) * mm, "end": v(-30.75, 22.38) * mm});
            skLineSegment(sketch, "E265", {"start": v(-30.75, 22.38) * mm, "end": v(-31.45, 22) * mm});
            skLineSegment(sketch, "E266", {"start": v(-31.45, 22) * mm, "end": v(-31.33, 22.77) * mm});
            skLineSegment(sketch, "E267", {"start": v(-31.33, 22.77) * mm, "end": v(-32, 23.35) * mm});
            skLineSegment(sketch, "E268", {"start": v(-42.42, 19.9) * mm, "end": v(-41.64, 19.9) * mm});
            skLineSegment(sketch, "E269", {"start": v(-41.64, 19.9) * mm, "end": v(-41.3, 20.62) * mm});
            skLineSegment(sketch, "E270", {"start": v(-41.3, 20.62) * mm, "end": v(-40.94, 19.9) * mm});
            skLineSegment(sketch, "E271", {"start": v(-40.94, 19.9) * mm, "end": v(-40.15, 19.9) * mm});
            skLineSegment(sketch, "E272", {"start": v(-40.15, 19.9) * mm, "end": v(-40.73, 19.38) * mm});
            skLineSegment(sketch, "E273", {"start": v(-40.73, 19.38) * mm, "end": v(-40.55, 18.54) * mm});
            skLineSegment(sketch, "E274", {"start": v(-40.55, 18.54) * mm, "end": v(-41.17, 18.93) * mm});
            skLineSegment(sketch, "E275", {"start": v(-41.17, 18.93) * mm, "end": v(-41.88, 18.54) * mm});
            skLineSegment(sketch, "E276", {"start": v(-41.88, 18.54) * mm, "end": v(-41.76, 19.32) * mm});
            skLineSegment(sketch, "E277", {"start": v(-41.76, 19.32) * mm, "end": v(-42.42, 19.9) * mm});
            skLineSegment(sketch, "E278", {"start": v(-35.25, 19.75) * mm, "end": v(-34.47, 19.75) * mm});
            skLineSegment(sketch, "E279", {"start": v(-34.47, 19.75) * mm, "end": v(-34.13, 20.46) * mm});
            skLineSegment(sketch, "E280", {"start": v(-34.13, 20.46) * mm, "end": v(-33.77, 19.75) * mm});
            skLineSegment(sketch, "E281", {"start": v(-33.77, 19.75) * mm, "end": v(-32.98, 19.75) * mm});
            skLineSegment(sketch, "E282", {"start": v(-32.98, 19.75) * mm, "end": v(-33.56, 19.22) * mm});
            skLineSegment(sketch, "E283", {"start": v(-33.56, 19.22) * mm, "end": v(-33.38, 18.39) * mm});
            skLineSegment(sketch, "E284", {"start": v(-33.38, 18.39) * mm, "end": v(-34, 18.77) * mm});
            skLineSegment(sketch, "E285", {"start": v(-34, 18.77) * mm, "end": v(-34.71, 18.39) * mm});
            skLineSegment(sketch, "E286", {"start": v(-34.71, 18.39) * mm, "end": v(-34.59, 19.17) * mm});
            skLineSegment(sketch, "E287", {"start": v(-34.59, 19.17) * mm, "end": v(-35.25, 19.75) * mm});
            skLineSegment(sketch, "E288", {"start": v(-28.31, 19.86) * mm, "end": v(-27.53, 19.86) * mm});
            skLineSegment(sketch, "E289", {"start": v(-27.53, 19.86) * mm, "end": v(-27.2, 20.58) * mm});
            skLineSegment(sketch, "E290", {"start": v(-27.2, 20.58) * mm, "end": v(-26.83, 19.86) * mm});
            skLineSegment(sketch, "E291", {"start": v(-26.83, 19.86) * mm, "end": v(-26.04, 19.86) * mm});
            skLineSegment(sketch, "E292", {"start": v(-26.04, 19.86) * mm, "end": v(-26.62, 19.34) * mm});
            skLineSegment(sketch, "E293", {"start": v(-26.62, 19.34) * mm, "end": v(-26.45, 18.5) * mm});
            skLineSegment(sketch, "E294", {"start": v(-26.45, 18.5) * mm, "end": v(-27.06, 18.89) * mm});
            skLineSegment(sketch, "E295", {"start": v(-27.06, 18.89) * mm, "end": v(-27.77, 18.5) * mm});
            skLineSegment(sketch, "E296", {"start": v(-27.77, 18.5) * mm, "end": v(-27.65, 19.29) * mm});
            skLineSegment(sketch, "E297", {"start": v(-27.65, 19.29) * mm, "end": v(-28.31, 19.86) * mm});
            skLineSegment(sketch, "E298", {"start": v(-21.26, 19.86) * mm, "end": v(-20.48, 19.86) * mm});
            skLineSegment(sketch, "E299", {"start": v(-20.48, 19.86) * mm, "end": v(-20.14, 20.58) * mm});
            skLineSegment(sketch, "E300", {"start": v(-20.14, 20.58) * mm, "end": v(-19.78, 19.86) * mm});
            skLineSegment(sketch, "E301", {"start": v(-19.78, 19.86) * mm, "end": v(-19, 19.86) * mm});
            skLineSegment(sketch, "E302", {"start": v(-19, 19.86) * mm, "end": v(-19.57, 19.34) * mm});
            skLineSegment(sketch, "E303", {"start": v(-19.57, 19.34) * mm, "end": v(-19.4, 18.5) * mm});
            skLineSegment(sketch, "E304", {"start": v(-19.4, 18.5) * mm, "end": v(-20.01, 18.89) * mm});
            skLineSegment(sketch, "E305", {"start": v(-20.01, 18.89) * mm, "end": v(-20.72, 18.5) * mm});
            skLineSegment(sketch, "E306", {"start": v(-20.72, 18.5) * mm, "end": v(-20.6, 19.29) * mm});
            skLineSegment(sketch, "E307", {"start": v(-20.6, 19.29) * mm, "end": v(-21.26, 19.86) * mm});
            skLineSegment(sketch, "E308", {"start": v(-14.48, 19.75) * mm, "end": v(-13.7, 19.75) * mm});
            skLineSegment(sketch, "E309", {"start": v(-13.7, 19.75) * mm, "end": v(-13.36, 20.46) * mm});
            skLineSegment(sketch, "E310", {"start": v(-13.36, 20.46) * mm, "end": v(-13, 19.75) * mm});
            skLineSegment(sketch, "E311", {"start": v(-13, 19.75) * mm, "end": v(-12.2, 19.75) * mm});
            skLineSegment(sketch, "E312", {"start": v(-12.2, 19.75) * mm, "end": v(-12.78, 19.22) * mm});
            skLineSegment(sketch, "E313", {"start": v(-12.78, 19.22) * mm, "end": v(-12.61, 18.39) * mm});
            skLineSegment(sketch, "E314", {"start": v(-12.61, 18.39) * mm, "end": v(-13.23, 18.77) * mm});
            skLineSegment(sketch, "E315", {"start": v(-13.23, 18.77) * mm, "end": v(-13.94, 18.39) * mm});
            skLineSegment(sketch, "E316", {"start": v(-13.94, 18.39) * mm, "end": v(-13.82, 19.17) * mm});
            skLineSegment(sketch, "E317", {"start": v(-13.82, 19.17) * mm, "end": v(-14.48, 19.75) * mm});
            skLineSegment(sketch, "E318", {"start": v(-10.91, 16.68) * mm, "end": v(-10.13, 16.68) * mm});
            skLineSegment(sketch, "E319", {"start": v(-10.13, 16.68) * mm, "end": v(-9.79, 17.4) * mm});
            skLineSegment(sketch, "E320", {"start": v(-9.79, 17.4) * mm, "end": v(-9.43, 16.68) * mm});
            skLineSegment(sketch, "E321", {"start": v(-9.43, 16.68) * mm, "end": v(-8.64, 16.68) * mm});
            skLineSegment(sketch, "E322", {"start": v(-8.64, 16.68) * mm, "end": v(-9.22, 16.16) * mm});
            skLineSegment(sketch, "E323", {"start": v(-9.22, 16.16) * mm, "end": v(-9.05, 15.32) * mm});
            skLineSegment(sketch, "E324", {"start": v(-9.05, 15.32) * mm, "end": v(-9.66, 15.71) * mm});
            skLineSegment(sketch, "E325", {"start": v(-9.66, 15.71) * mm, "end": v(-10.37, 15.32) * mm});
            skLineSegment(sketch, "E326", {"start": v(-10.37, 15.32) * mm, "end": v(-10.25, 16.1) * mm});
            skLineSegment(sketch, "E327", {"start": v(-10.25, 16.1) * mm, "end": v(-10.91, 16.68) * mm});
            skLineSegment(sketch, "E328", {"start": v(-17.89, 16.6) * mm, "end": v(-17.1, 16.6) * mm});
            skLineSegment(sketch, "E329", {"start": v(-17.1, 16.6) * mm, "end": v(-16.77, 17.32) * mm});
            skLineSegment(sketch, "E330", {"start": v(-16.77, 17.32) * mm, "end": v(-16.4, 16.6) * mm});
            skLineSegment(sketch, "E331", {"start": v(-16.4, 16.6) * mm, "end": v(-15.62, 16.6) * mm});
            skLineSegment(sketch, "E332", {"start": v(-15.62, 16.6) * mm, "end": v(-16.2, 16.08) * mm});
            skLineSegment(sketch, "E333", {"start": v(-16.2, 16.08) * mm, "end": v(-16.02, 15.25) * mm});
            skLineSegment(sketch, "E334", {"start": v(-16.02, 15.25) * mm, "end": v(-16.64, 15.63) * mm});
            skLineSegment(sketch, "E335", {"start": v(-16.64, 15.63) * mm, "end": v(-17.35, 15.25) * mm});
            skLineSegment(sketch, "E336", {"start": v(-17.35, 15.25) * mm, "end": v(-17.23, 16.03) * mm});
            skLineSegment(sketch, "E337", {"start": v(-17.23, 16.03) * mm, "end": v(-17.89, 16.6) * mm});
            skLineSegment(sketch, "E338", {"start": v(-24.94, 16.6) * mm, "end": v(-24.16, 16.6) * mm});
            skLineSegment(sketch, "E339", {"start": v(-24.16, 16.6) * mm, "end": v(-23.82, 17.32) * mm});
            skLineSegment(sketch, "E340", {"start": v(-23.82, 17.32) * mm, "end": v(-23.46, 16.6) * mm});
            skLineSegment(sketch, "E341", {"start": v(-23.46, 16.6) * mm, "end": v(-22.67, 16.6) * mm});
            skLineSegment(sketch, "E342", {"start": v(-22.67, 16.6) * mm, "end": v(-23.25, 16.08) * mm});
            skLineSegment(sketch, "E343", {"start": v(-23.25, 16.08) * mm, "end": v(-23.08, 15.25) * mm});
            skLineSegment(sketch, "E344", {"start": v(-23.08, 15.25) * mm, "end": v(-23.7, 15.63) * mm});
            skLineSegment(sketch, "E345", {"start": v(-23.7, 15.63) * mm, "end": v(-24.4, 15.25) * mm});
            skLineSegment(sketch, "E346", {"start": v(-24.4, 15.25) * mm, "end": v(-24.28, 16.03) * mm});
            skLineSegment(sketch, "E347", {"start": v(-24.28, 16.03) * mm, "end": v(-24.94, 16.6) * mm});
            skLineSegment(sketch, "E348", {"start": v(-31.96, 16.6) * mm, "end": v(-31.17, 16.6) * mm});
            skLineSegment(sketch, "E349", {"start": v(-31.17, 16.6) * mm, "end": v(-30.83, 17.32) * mm});
            skLineSegment(sketch, "E350", {"start": v(-30.83, 17.32) * mm, "end": v(-30.48, 16.6) * mm});
            skLineSegment(sketch, "E351", {"start": v(-30.48, 16.6) * mm, "end": v(-29.69, 16.6) * mm});
            skLineSegment(sketch, "E352", {"start": v(-29.69, 16.6) * mm, "end": v(-30.26, 16.08) * mm});
            skLineSegment(sketch, "E353", {"start": v(-30.26, 16.08) * mm, "end": v(-30.1, 15.25) * mm});
            skLineSegment(sketch, "E354", {"start": v(-30.1, 15.25) * mm, "end": v(-30.7, 15.63) * mm});
            skLineSegment(sketch, "E355", {"start": v(-30.7, 15.63) * mm, "end": v(-31.42, 15.25) * mm});
            skLineSegment(sketch, "E356", {"start": v(-31.42, 15.25) * mm, "end": v(-31.3, 16.03) * mm});
            skLineSegment(sketch, "E357", {"start": v(-31.3, 16.03) * mm, "end": v(-31.96, 16.6) * mm});
            skLineSegment(sketch, "E358", {"start": v(-38.9, 16.57) * mm, "end": v(-38.11, 16.57) * mm});
            skLineSegment(sketch, "E359", {"start": v(-38.11, 16.57) * mm, "end": v(-37.77, 17.28) * mm});
            skLineSegment(sketch, "E360", {"start": v(-37.77, 17.28) * mm, "end": v(-37.41, 16.57) * mm});
            skLineSegment(sketch, "E361", {"start": v(-37.41, 16.57) * mm, "end": v(-36.62, 16.57) * mm});
            skLineSegment(sketch, "E362", {"start": v(-36.62, 16.57) * mm, "end": v(-37.2, 16.04) * mm});
            skLineSegment(sketch, "E363", {"start": v(-37.2, 16.04) * mm, "end": v(-37.03, 15.2) * mm});
            skLineSegment(sketch, "E364", {"start": v(-37.03, 15.2) * mm, "end": v(-37.64, 15.6) * mm});
            skLineSegment(sketch, "E365", {"start": v(-37.64, 15.6) * mm, "end": v(-38.35, 15.2) * mm});
            skLineSegment(sketch, "E366", {"start": v(-38.35, 15.2) * mm, "end": v(-38.23, 16) * mm});
            skLineSegment(sketch, "E367", {"start": v(-38.23, 16) * mm, "end": v(-38.9, 16.57) * mm});
            skLineSegment(sketch, "E368", {"start": v(-45.83, 16.65) * mm, "end": v(-45.05, 16.65) * mm});
            skLineSegment(sketch, "E369", {"start": v(-45.05, 16.65) * mm, "end": v(-44.7, 17.36) * mm});
            skLineSegment(sketch, "E370", {"start": v(-44.7, 17.36) * mm, "end": v(-44.35, 16.65) * mm});
            skLineSegment(sketch, "E371", {"start": v(-44.35, 16.65) * mm, "end": v(-43.56, 16.65) * mm});
            skLineSegment(sketch, "E372", {"start": v(-43.56, 16.65) * mm, "end": v(-44.14, 16.12) * mm});
            skLineSegment(sketch, "E373", {"start": v(-44.14, 16.12) * mm, "end": v(-43.97, 15.29) * mm});
            skLineSegment(sketch, "E374", {"start": v(-43.97, 15.29) * mm, "end": v(-44.58, 15.67) * mm});
            skLineSegment(sketch, "E375", {"start": v(-44.58, 15.67) * mm, "end": v(-45.3, 15.29) * mm});
            skLineSegment(sketch, "E376", {"start": v(-45.3, 15.29) * mm, "end": v(-45.17, 16.07) * mm});
            skLineSegment(sketch, "E377", {"start": v(-45.17, 16.07) * mm, "end": v(-45.83, 16.65) * mm});
            skLineSegment(sketch, "E378", {"start": v(-14.44, 13.16) * mm, "end": v(-13.66, 13.16) * mm});
            skLineSegment(sketch, "E379", {"start": v(-13.66, 13.16) * mm, "end": v(-13.32, 13.87) * mm});
            skLineSegment(sketch, "E380", {"start": v(-13.32, 13.87) * mm, "end": v(-12.96, 13.16) * mm});
            skLineSegment(sketch, "E381", {"start": v(-12.96, 13.16) * mm, "end": v(-12.17, 13.16) * mm});
            skLineSegment(sketch, "E382", {"start": v(-12.17, 13.16) * mm, "end": v(-12.75, 12.63) * mm});
            skLineSegment(sketch, "E383", {"start": v(-12.75, 12.63) * mm, "end": v(-12.57, 11.8) * mm});
            skLineSegment(sketch, "E384", {"start": v(-12.57, 11.8) * mm, "end": v(-13.19, 12.18) * mm});
            skLineSegment(sketch, "E385", {"start": v(-13.19, 12.18) * mm, "end": v(-13.9, 11.8) * mm});
            skLineSegment(sketch, "E386", {"start": v(-13.9, 11.8) * mm, "end": v(-13.78, 12.58) * mm});
            skLineSegment(sketch, "E387", {"start": v(-13.78, 12.58) * mm, "end": v(-14.44, 13.16) * mm});
            skLineSegment(sketch, "E388", {"start": v(-21.42, 13.16) * mm, "end": v(-20.63, 13.16) * mm});
            skLineSegment(sketch, "E389", {"start": v(-20.63, 13.16) * mm, "end": v(-20.3, 13.87) * mm});
            skLineSegment(sketch, "E390", {"start": v(-20.3, 13.87) * mm, "end": v(-19.94, 13.16) * mm});
            skLineSegment(sketch, "E391", {"start": v(-19.94, 13.16) * mm, "end": v(-19.15, 13.16) * mm});
            skLineSegment(sketch, "E392", {"start": v(-19.15, 13.16) * mm, "end": v(-19.72, 12.63) * mm});
            skLineSegment(sketch, "E393", {"start": v(-19.72, 12.63) * mm, "end": v(-19.55, 11.8) * mm});
            skLineSegment(sketch, "E394", {"start": v(-19.55, 11.8) * mm, "end": v(-20.17, 12.18) * mm});
            skLineSegment(sketch, "E395", {"start": v(-20.17, 12.18) * mm, "end": v(-20.87, 11.8) * mm});
            skLineSegment(sketch, "E396", {"start": v(-20.87, 11.8) * mm, "end": v(-20.75, 12.58) * mm});
            skLineSegment(sketch, "E397", {"start": v(-20.75, 12.58) * mm, "end": v(-21.42, 13.16) * mm});
            skLineSegment(sketch, "E398", {"start": v(-28.47, 13.2) * mm, "end": v(-27.69, 13.2) * mm});
            skLineSegment(sketch, "E399", {"start": v(-27.69, 13.2) * mm, "end": v(-27.35, 13.91) * mm});
            skLineSegment(sketch, "E400", {"start": v(-27.35, 13.91) * mm, "end": v(-26.99, 13.2) * mm});
            skLineSegment(sketch, "E401", {"start": v(-26.99, 13.2) * mm, "end": v(-26.2, 13.2) * mm});
            skLineSegment(sketch, "E402", {"start": v(-26.2, 13.2) * mm, "end": v(-26.78, 12.67) * mm});
            skLineSegment(sketch, "E403", {"start": v(-26.78, 12.67) * mm, "end": v(-26.6, 11.84) * mm});
            skLineSegment(sketch, "E404", {"start": v(-26.6, 11.84) * mm, "end": v(-27.22, 12.22) * mm});
            skLineSegment(sketch, "E405", {"start": v(-27.22, 12.22) * mm, "end": v(-27.93, 11.84) * mm});
            skLineSegment(sketch, "E406", {"start": v(-27.93, 11.84) * mm, "end": v(-27.8, 12.62) * mm});
            skLineSegment(sketch, "E407", {"start": v(-27.8, 12.62) * mm, "end": v(-28.47, 13.2) * mm});
            skLineSegment(sketch, "E408", {"start": v(-35.4, 13.2) * mm, "end": v(-34.62, 13.2) * mm});
            skLineSegment(sketch, "E409", {"start": v(-34.62, 13.2) * mm, "end": v(-34.28, 13.91) * mm});
            skLineSegment(sketch, "E410", {"start": v(-34.28, 13.91) * mm, "end": v(-33.93, 13.2) * mm});
            skLineSegment(sketch, "E411", {"start": v(-33.93, 13.2) * mm, "end": v(-33.14, 13.2) * mm});
            skLineSegment(sketch, "E412", {"start": v(-33.14, 13.2) * mm, "end": v(-33.71, 12.67) * mm});
            skLineSegment(sketch, "E413", {"start": v(-33.71, 12.67) * mm, "end": v(-33.54, 11.84) * mm});
            skLineSegment(sketch, "E414", {"start": v(-33.54, 11.84) * mm, "end": v(-34.16, 12.22) * mm});
            skLineSegment(sketch, "E415", {"start": v(-34.16, 12.22) * mm, "end": v(-34.87, 11.84) * mm});
            skLineSegment(sketch, "E416", {"start": v(-34.87, 11.84) * mm, "end": v(-34.74, 12.62) * mm});
            skLineSegment(sketch, "E417", {"start": v(-34.74, 12.62) * mm, "end": v(-35.4, 13.2) * mm});
            skLineSegment(sketch, "E418", {"start": v(-42.38, 13.16) * mm, "end": v(-41.6, 13.16) * mm});
            skLineSegment(sketch, "E419", {"start": v(-41.6, 13.16) * mm, "end": v(-41.26, 13.87) * mm});
            skLineSegment(sketch, "E420", {"start": v(-41.26, 13.87) * mm, "end": v(-40.9, 13.16) * mm});
            skLineSegment(sketch, "E421", {"start": v(-40.9, 13.16) * mm, "end": v(-40.11, 13.16) * mm});
            skLineSegment(sketch, "E422", {"start": v(-40.11, 13.16) * mm, "end": v(-40.69, 12.63) * mm});
            skLineSegment(sketch, "E423", {"start": v(-40.69, 12.63) * mm, "end": v(-40.52, 11.8) * mm});
            skLineSegment(sketch, "E424", {"start": v(-40.52, 11.8) * mm, "end": v(-41.13, 12.18) * mm});
            skLineSegment(sketch, "E425", {"start": v(-41.13, 12.18) * mm, "end": v(-41.84, 11.8) * mm});
            skLineSegment(sketch, "E426", {"start": v(-41.84, 11.8) * mm, "end": v(-41.72, 12.58) * mm});
            skLineSegment(sketch, "E427", {"start": v(-41.72, 12.58) * mm, "end": v(-42.38, 13.16) * mm});
            skLineSegment(sketch, "E428", {"start": v(-45.87, 9.86) * mm, "end": v(-45.09, 9.86) * mm});
            skLineSegment(sketch, "E429", {"start": v(-45.09, 9.86) * mm, "end": v(-44.75, 10.58) * mm});
            skLineSegment(sketch, "E430", {"start": v(-44.75, 10.58) * mm, "end": v(-44.4, 9.86) * mm});
            skLineSegment(sketch, "E431", {"start": v(-44.4, 9.86) * mm, "end": v(-43.6, 9.86) * mm});
            skLineSegment(sketch, "E432", {"start": v(-43.6, 9.86) * mm, "end": v(-44.18, 9.34) * mm});
            skLineSegment(sketch, "E433", {"start": v(-44.18, 9.34) * mm, "end": v(-44, 8.5) * mm});
            skLineSegment(sketch, "E434", {"start": v(-44, 8.5) * mm, "end": v(-44.62, 8.89) * mm});
            skLineSegment(sketch, "E435", {"start": v(-44.62, 8.89) * mm, "end": v(-45.33, 8.5) * mm});
            skLineSegment(sketch, "E436", {"start": v(-45.33, 8.5) * mm, "end": v(-45.2, 9.29) * mm});
            skLineSegment(sketch, "E437", {"start": v(-45.2, 9.29) * mm, "end": v(-45.87, 9.86) * mm});
            skLineSegment(sketch, "E438", {"start": v(-38.9, 10.02) * mm, "end": v(-38.11, 10.02) * mm});
            skLineSegment(sketch, "E439", {"start": v(-38.11, 10.02) * mm, "end": v(-37.77, 10.73) * mm});
            skLineSegment(sketch, "E440", {"start": v(-37.77, 10.73) * mm, "end": v(-37.41, 10.02) * mm});
            skLineSegment(sketch, "E441", {"start": v(-37.41, 10.02) * mm, "end": v(-36.62, 10.02) * mm});
            skLineSegment(sketch, "E442", {"start": v(-36.62, 10.02) * mm, "end": v(-37.2, 9.5) * mm});
            skLineSegment(sketch, "E443", {"start": v(-37.2, 9.5) * mm, "end": v(-37.03, 8.66) * mm});
            skLineSegment(sketch, "E444", {"start": v(-37.03, 8.66) * mm, "end": v(-37.64, 9.04) * mm});
            skLineSegment(sketch, "E445", {"start": v(-37.64, 9.04) * mm, "end": v(-38.35, 8.66) * mm});
            skLineSegment(sketch, "E446", {"start": v(-38.35, 8.66) * mm, "end": v(-38.23, 9.44) * mm});
            skLineSegment(sketch, "E447", {"start": v(-38.23, 9.44) * mm, "end": v(-38.9, 10.02) * mm});
            skLineSegment(sketch, "E448", {"start": v(-31.88, 9.9) * mm, "end": v(-31.1, 9.9) * mm});
            skLineSegment(sketch, "E449", {"start": v(-31.1, 9.9) * mm, "end": v(-30.76, 10.62) * mm});
            skLineSegment(sketch, "E450", {"start": v(-30.76, 10.62) * mm, "end": v(-30.4, 9.9) * mm});
            skLineSegment(sketch, "E451", {"start": v(-30.4, 9.9) * mm, "end": v(-29.6, 9.9) * mm});
            skLineSegment(sketch, "E452", {"start": v(-29.6, 9.9) * mm, "end": v(-30.19, 9.38) * mm});
            skLineSegment(sketch, "E453", {"start": v(-30.19, 9.38) * mm, "end": v(-30.01, 8.54) * mm});
            skLineSegment(sketch, "E454", {"start": v(-30.01, 8.54) * mm, "end": v(-30.63, 8.93) * mm});
            skLineSegment(sketch, "E455", {"start": v(-30.63, 8.93) * mm, "end": v(-31.34, 8.54) * mm});
            skLineSegment(sketch, "E456", {"start": v(-31.34, 8.54) * mm, "end": v(-31.22, 9.33) * mm});
            skLineSegment(sketch, "E457", {"start": v(-31.22, 9.33) * mm, "end": v(-31.88, 9.9) * mm});
            skLineSegment(sketch, "E458", {"start": v(-24.87, 9.9) * mm, "end": v(-24.08, 9.9) * mm});
            skLineSegment(sketch, "E459", {"start": v(-24.08, 9.9) * mm, "end": v(-23.74, 10.62) * mm});
            skLineSegment(sketch, "E460", {"start": v(-23.74, 10.62) * mm, "end": v(-23.38, 9.9) * mm});
            skLineSegment(sketch, "E461", {"start": v(-23.38, 9.9) * mm, "end": v(-22.6, 9.9) * mm});
            skLineSegment(sketch, "E462", {"start": v(-22.6, 9.9) * mm, "end": v(-23.17, 9.38) * mm});
            skLineSegment(sketch, "E463", {"start": v(-23.17, 9.38) * mm, "end": v(-23, 8.54) * mm});
            skLineSegment(sketch, "E464", {"start": v(-23, 8.54) * mm, "end": v(-23.61, 8.93) * mm});
            skLineSegment(sketch, "E465", {"start": v(-23.61, 8.93) * mm, "end": v(-24.32, 8.54) * mm});
            skLineSegment(sketch, "E466", {"start": v(-24.32, 8.54) * mm, "end": v(-24.2, 9.33) * mm});
            skLineSegment(sketch, "E467", {"start": v(-24.2, 9.33) * mm, "end": v(-24.87, 9.9) * mm});
            skLineSegment(sketch, "E468", {"start": v(-28.4, 6.41) * mm, "end": v(-27.6, 6.41) * mm});
            skLineSegment(sketch, "E469", {"start": v(-27.6, 6.41) * mm, "end": v(-27.27, 7.13) * mm});
            skLineSegment(sketch, "E470", {"start": v(-27.27, 7.13) * mm, "end": v(-26.91, 6.41) * mm});
            skLineSegment(sketch, "E471", {"start": v(-26.91, 6.41) * mm, "end": v(-26.12, 6.41) * mm});
            skLineSegment(sketch, "E472", {"start": v(-26.12, 6.41) * mm, "end": v(-26.7, 5.89) * mm});
            skLineSegment(sketch, "E473", {"start": v(-26.7, 5.89) * mm, "end": v(-26.53, 5.05) * mm});
            skLineSegment(sketch, "E474", {"start": v(-26.53, 5.05) * mm, "end": v(-27.14, 5.44) * mm});
            skLineSegment(sketch, "E475", {"start": v(-27.14, 5.44) * mm, "end": v(-27.85, 5.05) * mm});
            skLineSegment(sketch, "E476", {"start": v(-27.85, 5.05) * mm, "end": v(-27.73, 5.84) * mm});
            skLineSegment(sketch, "E477", {"start": v(-27.73, 5.84) * mm, "end": v(-28.4, 6.41) * mm});
            skLineSegment(sketch, "E478", {"start": v(-35.4, 6.41) * mm, "end": v(-34.62, 6.41) * mm});
            skLineSegment(sketch, "E479", {"start": v(-34.62, 6.41) * mm, "end": v(-34.28, 7.13) * mm});
            skLineSegment(sketch, "E480", {"start": v(-34.28, 7.13) * mm, "end": v(-33.93, 6.41) * mm});
            skLineSegment(sketch, "E481", {"start": v(-33.93, 6.41) * mm, "end": v(-33.14, 6.41) * mm});
            skLineSegment(sketch, "E482", {"start": v(-33.14, 6.41) * mm, "end": v(-33.71, 5.89) * mm});
            skLineSegment(sketch, "E483", {"start": v(-33.71, 5.89) * mm, "end": v(-33.54, 5.05) * mm});
            skLineSegment(sketch, "E484", {"start": v(-33.54, 5.05) * mm, "end": v(-34.16, 5.44) * mm});
            skLineSegment(sketch, "E485", {"start": v(-34.16, 5.44) * mm, "end": v(-34.87, 5.05) * mm});
            skLineSegment(sketch, "E486", {"start": v(-34.87, 5.05) * mm, "end": v(-34.74, 5.84) * mm});
            skLineSegment(sketch, "E487", {"start": v(-34.74, 5.84) * mm, "end": v(-35.4, 6.41) * mm});
            skLineSegment(sketch, "E488", {"start": v(-42.34, 6.34) * mm, "end": v(-41.56, 6.34) * mm});
            skLineSegment(sketch, "E489", {"start": v(-41.56, 6.34) * mm, "end": v(-41.22, 7.05) * mm});
            skLineSegment(sketch, "E490", {"start": v(-41.22, 7.05) * mm, "end": v(-40.86, 6.34) * mm});
            skLineSegment(sketch, "E491", {"start": v(-40.86, 6.34) * mm, "end": v(-40.07, 6.34) * mm});
            skLineSegment(sketch, "E492", {"start": v(-40.07, 6.34) * mm, "end": v(-40.65, 5.81) * mm});
            skLineSegment(sketch, "E493", {"start": v(-40.65, 5.81) * mm, "end": v(-40.48, 4.98) * mm});
            skLineSegment(sketch, "E494", {"start": v(-40.48, 4.98) * mm, "end": v(-41.1, 5.36) * mm});
            skLineSegment(sketch, "E495", {"start": v(-41.1, 5.36) * mm, "end": v(-41.8, 4.98) * mm});
            skLineSegment(sketch, "E496", {"start": v(-41.8, 4.98) * mm, "end": v(-41.68, 5.76) * mm});
            skLineSegment(sketch, "E497", {"start": v(-41.68, 5.76) * mm, "end": v(-42.34, 6.34) * mm});
            skLineSegment(sketch, "E498", {"start": v(-45.83, 3.58) * mm, "end": v(-45.05, 3.58) * mm});
            skLineSegment(sketch, "E499", {"start": v(-45.05, 3.58) * mm, "end": v(-44.7, 4.3) * mm});
            skLineSegment(sketch, "E500", {"start": v(-44.7, 4.3) * mm, "end": v(-44.35, 3.58) * mm});
            skLineSegment(sketch, "E501", {"start": v(-44.35, 3.58) * mm, "end": v(-43.56, 3.58) * mm});
            skLineSegment(sketch, "E502", {"start": v(-43.56, 3.58) * mm, "end": v(-44.14, 3.06) * mm});
            skLineSegment(sketch, "E503", {"start": v(-44.14, 3.06) * mm, "end": v(-43.97, 2.22) * mm});
            skLineSegment(sketch, "E504", {"start": v(-43.97, 2.22) * mm, "end": v(-44.58, 2.61) * mm});
            skLineSegment(sketch, "E505", {"start": v(-44.58, 2.61) * mm, "end": v(-45.3, 2.22) * mm});
            skLineSegment(sketch, "E506", {"start": v(-45.3, 2.22) * mm, "end": v(-45.17, 3) * mm});
            skLineSegment(sketch, "E507", {"start": v(-45.17, 3) * mm, "end": v(-45.83, 3.58) * mm});
            skLineSegment(sketch, "E508", {"start": v(-38.82, 3.66) * mm, "end": v(-38.03, 3.66) * mm});
            skLineSegment(sketch, "E509", {"start": v(-38.03, 3.66) * mm, "end": v(-37.7, 4.38) * mm});
            skLineSegment(sketch, "E510", {"start": v(-37.7, 4.38) * mm, "end": v(-37.34, 3.66) * mm});
            skLineSegment(sketch, "E511", {"start": v(-37.34, 3.66) * mm, "end": v(-36.55, 3.66) * mm});
            skLineSegment(sketch, "E512", {"start": v(-36.55, 3.66) * mm, "end": v(-37.12, 3.14) * mm});
            skLineSegment(sketch, "E513", {"start": v(-37.12, 3.14) * mm, "end": v(-36.95, 2.3) * mm});
            skLineSegment(sketch, "E514", {"start": v(-36.95, 2.3) * mm, "end": v(-37.57, 2.69) * mm});
            skLineSegment(sketch, "E515", {"start": v(-37.57, 2.69) * mm, "end": v(-38.28, 2.3) * mm});
            skLineSegment(sketch, "E516", {"start": v(-38.28, 2.3) * mm, "end": v(-38.15, 3.09) * mm});
            skLineSegment(sketch, "E517", {"start": v(-38.15, 3.09) * mm, "end": v(-38.82, 3.66) * mm});
            skLineSegment(sketch, "E518", {"start": v(-31.92, 3.58) * mm, "end": v(-31.14, 3.58) * mm});
            skLineSegment(sketch, "E519", {"start": v(-31.14, 3.58) * mm, "end": v(-30.8, 4.3) * mm});
            skLineSegment(sketch, "E520", {"start": v(-30.8, 4.3) * mm, "end": v(-30.44, 3.58) * mm});
            skLineSegment(sketch, "E521", {"start": v(-30.44, 3.58) * mm, "end": v(-29.65, 3.58) * mm});
            skLineSegment(sketch, "E522", {"start": v(-29.65, 3.58) * mm, "end": v(-30.22, 3.06) * mm});
            skLineSegment(sketch, "E523", {"start": v(-30.22, 3.06) * mm, "end": v(-30.05, 2.22) * mm});
            skLineSegment(sketch, "E524", {"start": v(-30.05, 2.22) * mm, "end": v(-30.67, 2.61) * mm});
            skLineSegment(sketch, "E525", {"start": v(-30.67, 2.61) * mm, "end": v(-31.38, 2.22) * mm});
            skLineSegment(sketch, "E526", {"start": v(-31.38, 2.22) * mm, "end": v(-31.26, 3) * mm});
            skLineSegment(sketch, "E527", {"start": v(-31.26, 3) * mm, "end": v(-31.92, 3.58) * mm});
            skSolve(sketch);
        }
        {
            var Q0;
            {var subQ0=sQuery(id+"F4.wireOp",EDGE,"E6.top");Q0=makeQuery(id+"F4.imprint","IMPRINT",FACE,{"disambiguationData":[TD([[makeQuery(id+"F4.imprint","IMPRINT",EDGE,{"derivedFrom":subQ0}),-1.0]])]});}
            var Q1;
            {var subQ2=sQuery(id+"F4.wireOp",EDGE,"E10.bottom");Q1=makeQuery(id+"F4.imprint","IMPRINT",FACE,{"disambiguationData":[TD([[makeQuery(id+"F4.imprint","IMPRINT",EDGE,{"derivedFrom":subQ2}),1.0]])]});}
            var Q2;
            {var subQ0=sQuery(id+"F4.wireOp",EDGE,"E14.right");Q2=makeQuery(id+"F4.imprint","IMPRINT",FACE,{"disambiguationData":[TD([[makeQuery(id+"F4.imprint","IMPRINT",EDGE,{"derivedFrom":subQ0}),-1.0]])]});}
            var Q3;
            Q3=makeQuery(id+"F4.imprint","IMPRINT",FACE,{"disambiguationData":[TD([[makeQuery(id+"F4.imprint","IMPRINT",EDGE,{"derivedFrom":sQuery(id+"F4.wireOp",EDGE,"E17.bottom")}),1.0]])]});
            var Q4;
            Q4=makeQuery(id+"F4.imprint","IMPRINT",FACE,{"disambiguationData":[TD([[makeQuery(id+"F4.imprint","IMPRINT",EDGE,{"derivedFrom":sQuery(id+"F4.wireOp",EDGE,"E20.top")}),-1.0]])]});
            var Q5;
            {var subQ0=sQuery(id+"F4.wireOp",EDGE,"E22.top");Q5=makeQuery(id+"F4.imprint","IMPRINT",FACE,{"disambiguationData":[TD([[makeQuery(id+"F4.imprint","IMPRINT",EDGE,{"derivedFrom":subQ0}),1.0]])]});}
            var Q6;
            Q6=makeQuery(id+"F4.imprint","IMPRINT",FACE,{"disambiguationData":[TD([[makeQuery(id+"F4.imprint","IMPRINT",EDGE,{"derivedFrom":sQuery(id+"F4.wireOp",EDGE,"E28")}),-1.0]])]});
            var Q7;
            Q7=makeQuery(id+"F4.imprint","IMPRINT",FACE,{"disambiguationData":[TD([[makeQuery(id+"F4.imprint","IMPRINT",EDGE,{"derivedFrom":sQuery(id+"F4.wireOp",EDGE,"E38")}),-1.0]])]});
            var Q8;
            Q8=makeQuery(id+"F4.imprint","IMPRINT",FACE,{"disambiguationData":[TD([[makeQuery(id+"F4.imprint","IMPRINT",EDGE,{"derivedFrom":sQuery(id+"F4.wireOp",EDGE,"E158")}),-1.0]])]});
            var Q9;
            Q9=makeQuery(id+"F4.imprint","IMPRINT",FACE,{"disambiguationData":[TD([[makeQuery(id+"F4.imprint","IMPRINT",EDGE,{"derivedFrom":sQuery(id+"F4.wireOp",EDGE,"E178")}),-1.0]])]});
            var Q10;
            Q10=makeQuery(id+"F4.imprint","IMPRINT",FACE,{"disambiguationData":[TD([[makeQuery(id+"F4.imprint","IMPRINT",EDGE,{"derivedFrom":sQuery(id+"F4.wireOp",EDGE,"E198")}),-1.0]])]});
            var Q11;
            Q11=makeQuery(id+"F4.imprint","IMPRINT",FACE,{"disambiguationData":[TD([[makeQuery(id+"F4.imprint","IMPRINT",EDGE,{"derivedFrom":sQuery(id+"F4.wireOp",EDGE,"E218")}),-1.0]])]});
            var Q12;
            Q12=makeQuery(id+"F4.imprint","IMPRINT",FACE,{"disambiguationData":[TD([[makeQuery(id+"F4.imprint","IMPRINT",EDGE,{"derivedFrom":sQuery(id+"F4.wireOp",EDGE,"E208")}),-1.0]])]});
            var Q13;
            Q13=makeQuery(id+"F4.imprint","IMPRINT",FACE,{"disambiguationData":[TD([[makeQuery(id+"F4.imprint","IMPRINT",EDGE,{"derivedFrom":sQuery(id+"F4.wireOp",EDGE,"E188")}),-1.0]])]});
            var Q14;
            Q14=makeQuery(id+"F4.imprint","IMPRINT",FACE,{"disambiguationData":[TD([[makeQuery(id+"F4.imprint","IMPRINT",EDGE,{"derivedFrom":sQuery(id+"F4.wireOp",EDGE,"E168")}),-1.0]])]});
            var Q15;
            Q15=makeQuery(id+"F4.imprint","IMPRINT",FACE,{"disambiguationData":[TD([[makeQuery(id+"F4.imprint","IMPRINT",EDGE,{"derivedFrom":sQuery(id+"F4.wireOp",EDGE,"E148")}),-1.0]])]});
            var Q16;
            Q16=makeQuery(id+"F4.imprint","IMPRINT",FACE,{"disambiguationData":[TD([[makeQuery(id+"F4.imprint","IMPRINT",EDGE,{"derivedFrom":sQuery(id+"F4.wireOp",EDGE,"E118")}),-1.0]])]});
            var Q17;
            Q17=makeQuery(id+"F4.imprint","IMPRINT",FACE,{"disambiguationData":[TD([[makeQuery(id+"F4.imprint","IMPRINT",EDGE,{"derivedFrom":sQuery(id+"F4.wireOp",EDGE,"E128")}),-1.0]])]});
            var Q18;
            Q18=makeQuery(id+"F4.imprint","IMPRINT",FACE,{"disambiguationData":[TD([[makeQuery(id+"F4.imprint","IMPRINT",EDGE,{"derivedFrom":sQuery(id+"F4.wireOp",EDGE,"E138")}),-1.0]])]});
            var Q19;
            Q19=makeQuery(id+"F4.imprint","IMPRINT",FACE,{"disambiguationData":[TD([[makeQuery(id+"F4.imprint","IMPRINT",EDGE,{"derivedFrom":sQuery(id+"F4.wireOp",EDGE,"E258")}),-1.0]])]});
            var Q20;
            Q20=makeQuery(id+"F4.imprint","IMPRINT",FACE,{"disambiguationData":[TD([[makeQuery(id+"F4.imprint","IMPRINT",EDGE,{"derivedFrom":sQuery(id+"F4.wireOp",EDGE,"E248")}),-1.0]])]});
            var Q21;
            Q21=makeQuery(id+"F4.imprint","IMPRINT",FACE,{"disambiguationData":[TD([[makeQuery(id+"F4.imprint","IMPRINT",EDGE,{"derivedFrom":sQuery(id+"F4.wireOp",EDGE,"E238")}),-1.0]])]});
            var Q22;
            Q22=makeQuery(id+"F4.imprint","IMPRINT",FACE,{"disambiguationData":[TD([[makeQuery(id+"F4.imprint","IMPRINT",EDGE,{"derivedFrom":sQuery(id+"F4.wireOp",EDGE,"E228")}),-1.0]])]});
            var Q23;
            Q23=makeQuery(id+"F4.imprint","IMPRINT",FACE,{"disambiguationData":[TD([[makeQuery(id+"F4.imprint","IMPRINT",EDGE,{"derivedFrom":sQuery(id+"F4.wireOp",EDGE,"E268")}),-1.0]])]});
            var Q24;
            Q24=makeQuery(id+"F4.imprint","IMPRINT",FACE,{"disambiguationData":[TD([[makeQuery(id+"F4.imprint","IMPRINT",EDGE,{"derivedFrom":sQuery(id+"F4.wireOp",EDGE,"E278")}),-1.0]])]});
            var Q25;
            Q25=makeQuery(id+"F4.imprint","IMPRINT",FACE,{"disambiguationData":[TD([[makeQuery(id+"F4.imprint","IMPRINT",EDGE,{"derivedFrom":sQuery(id+"F4.wireOp",EDGE,"E288")}),-1.0]])]});
            var Q26;
            Q26=makeQuery(id+"F4.imprint","IMPRINT",FACE,{"disambiguationData":[TD([[makeQuery(id+"F4.imprint","IMPRINT",EDGE,{"derivedFrom":sQuery(id+"F4.wireOp",EDGE,"E298")}),-1.0]])]});
            var Q27;
            Q27=makeQuery(id+"F4.imprint","IMPRINT",FACE,{"disambiguationData":[TD([[makeQuery(id+"F4.imprint","IMPRINT",EDGE,{"derivedFrom":sQuery(id+"F4.wireOp",EDGE,"E308")}),-1.0]])]});
            var Q28;
            Q28=makeQuery(id+"F4.imprint","IMPRINT",FACE,{"disambiguationData":[TD([[makeQuery(id+"F4.imprint","IMPRINT",EDGE,{"derivedFrom":sQuery(id+"F4.wireOp",EDGE,"E368")}),-1.0]])]});
            var Q29;
            Q29=makeQuery(id+"F4.imprint","IMPRINT",FACE,{"disambiguationData":[TD([[makeQuery(id+"F4.imprint","IMPRINT",EDGE,{"derivedFrom":sQuery(id+"F4.wireOp",EDGE,"E358")}),-1.0]])]});
            var Q30;
            Q30=makeQuery(id+"F4.imprint","IMPRINT",FACE,{"disambiguationData":[TD([[makeQuery(id+"F4.imprint","IMPRINT",EDGE,{"derivedFrom":sQuery(id+"F4.wireOp",EDGE,"E348")}),-1.0]])]});
            var Q31;
            Q31=makeQuery(id+"F4.imprint","IMPRINT",FACE,{"disambiguationData":[TD([[makeQuery(id+"F4.imprint","IMPRINT",EDGE,{"derivedFrom":sQuery(id+"F4.wireOp",EDGE,"E338")}),-1.0]])]});
            var Q32;
            Q32=makeQuery(id+"F4.imprint","IMPRINT",FACE,{"disambiguationData":[TD([[makeQuery(id+"F4.imprint","IMPRINT",EDGE,{"derivedFrom":sQuery(id+"F4.wireOp",EDGE,"E328")}),-1.0]])]});
            var Q33;
            Q33=makeQuery(id+"F4.imprint","IMPRINT",FACE,{"disambiguationData":[TD([[makeQuery(id+"F4.imprint","IMPRINT",EDGE,{"derivedFrom":sQuery(id+"F4.wireOp",EDGE,"E318")}),-1.0]])]});
            var Q34;
            Q34=makeQuery(id+"F4.imprint","IMPRINT",FACE,{"disambiguationData":[TD([[makeQuery(id+"F4.imprint","IMPRINT",EDGE,{"derivedFrom":sQuery(id+"F4.wireOp",EDGE,"E378")}),-1.0]])]});
            var Q35;
            Q35=makeQuery(id+"F4.imprint","IMPRINT",FACE,{"disambiguationData":[TD([[makeQuery(id+"F4.imprint","IMPRINT",EDGE,{"derivedFrom":sQuery(id+"F4.wireOp",EDGE,"E388")}),-1.0]])]});
            var Q36;
            Q36=makeQuery(id+"F4.imprint","IMPRINT",FACE,{"disambiguationData":[TD([[makeQuery(id+"F4.imprint","IMPRINT",EDGE,{"derivedFrom":sQuery(id+"F4.wireOp",EDGE,"E398")}),-1.0]])]});
            var Q37;
            Q37=makeQuery(id+"F4.imprint","IMPRINT",FACE,{"disambiguationData":[TD([[makeQuery(id+"F4.imprint","IMPRINT",EDGE,{"derivedFrom":sQuery(id+"F4.wireOp",EDGE,"E408")}),-1.0]])]});
            var Q38;
            Q38=makeQuery(id+"F4.imprint","IMPRINT",FACE,{"disambiguationData":[TD([[makeQuery(id+"F4.imprint","IMPRINT",EDGE,{"derivedFrom":sQuery(id+"F4.wireOp",EDGE,"E418")}),-1.0]])]});
            var Q39;
            Q39=makeQuery(id+"F4.imprint","IMPRINT",FACE,{"disambiguationData":[TD([[makeQuery(id+"F4.imprint","IMPRINT",EDGE,{"derivedFrom":sQuery(id+"F4.wireOp",EDGE,"E428")}),-1.0]])]});
            var Q40;
            Q40=makeQuery(id+"F4.imprint","IMPRINT",FACE,{"disambiguationData":[TD([[makeQuery(id+"F4.imprint","IMPRINT",EDGE,{"derivedFrom":sQuery(id+"F4.wireOp",EDGE,"E438")}),-1.0]])]});
            var Q41;
            Q41=makeQuery(id+"F4.imprint","IMPRINT",FACE,{"disambiguationData":[TD([[makeQuery(id+"F4.imprint","IMPRINT",EDGE,{"derivedFrom":sQuery(id+"F4.wireOp",EDGE,"E448")}),-1.0]])]});
            var Q42;
            Q42=makeQuery(id+"F4.imprint","IMPRINT",FACE,{"disambiguationData":[TD([[makeQuery(id+"F4.imprint","IMPRINT",EDGE,{"derivedFrom":sQuery(id+"F4.wireOp",EDGE,"E458")}),-1.0]])]});
            var Q43;
            Q43=makeQuery(id+"F4.imprint","IMPRINT",FACE,{"disambiguationData":[TD([[makeQuery(id+"F4.imprint","IMPRINT",EDGE,{"derivedFrom":sQuery(id+"F4.wireOp",EDGE,"E98")}),-1.0]])]});
            var Q44;
            Q44=makeQuery(id+"F4.imprint","IMPRINT",FACE,{"disambiguationData":[TD([[makeQuery(id+"F4.imprint","IMPRINT",EDGE,{"derivedFrom":sQuery(id+"F4.wireOp",EDGE,"E88")}),-1.0]])]});
            var Q45;
            Q45=makeQuery(id+"F4.imprint","IMPRINT",FACE,{"disambiguationData":[TD([[makeQuery(id+"F4.imprint","IMPRINT",EDGE,{"derivedFrom":sQuery(id+"F4.wireOp",EDGE,"E68")}),-1.0]])]});
            var Q46;
            Q46=makeQuery(id+"F4.imprint","IMPRINT",FACE,{"disambiguationData":[TD([[makeQuery(id+"F4.imprint","IMPRINT",EDGE,{"derivedFrom":sQuery(id+"F4.wireOp",EDGE,"E48")}),-1.0]])]});
            var Q47;
            Q47=makeQuery(id+"F4.imprint","IMPRINT",FACE,{"disambiguationData":[TD([[makeQuery(id+"F4.imprint","IMPRINT",EDGE,{"derivedFrom":sQuery(id+"F4.wireOp",EDGE,"E468")}),-1.0]])]});
            var Q48;
            Q48=makeQuery(id+"F4.imprint","IMPRINT",FACE,{"disambiguationData":[TD([[makeQuery(id+"F4.imprint","IMPRINT",EDGE,{"derivedFrom":sQuery(id+"F4.wireOp",EDGE,"E478")}),-1.0]])]});
            var Q49;
            Q49=makeQuery(id+"F4.imprint","IMPRINT",FACE,{"disambiguationData":[TD([[makeQuery(id+"F4.imprint","IMPRINT",EDGE,{"derivedFrom":sQuery(id+"F4.wireOp",EDGE,"E488")}),-1.0]])]});
            var Q50;
            Q50=makeQuery(id+"F4.imprint","IMPRINT",FACE,{"disambiguationData":[TD([[makeQuery(id+"F4.imprint","IMPRINT",EDGE,{"derivedFrom":sQuery(id+"F4.wireOp",EDGE,"E498")}),-1.0]])]});
            var Q51;
            Q51=makeQuery(id+"F4.imprint","IMPRINT",FACE,{"disambiguationData":[TD([[makeQuery(id+"F4.imprint","IMPRINT",EDGE,{"derivedFrom":sQuery(id+"F4.wireOp",EDGE,"E508")}),-1.0]])]});
            var Q52;
            Q52=makeQuery(id+"F4.imprint","IMPRINT",FACE,{"disambiguationData":[TD([[makeQuery(id+"F4.imprint","IMPRINT",EDGE,{"derivedFrom":sQuery(id+"F4.wireOp",EDGE,"E518")}),-1.0]])]});
            var Q53;
            Q53=makeQuery(id+"F4.imprint","IMPRINT",FACE,{"disambiguationData":[TD([[makeQuery(id+"F4.imprint","IMPRINT",EDGE,{"derivedFrom":sQuery(id+"F4.wireOp",EDGE,"E108")}),-1.0]])]});
            var Q54;
            Q54=makeQuery(id+"F4.imprint","IMPRINT",FACE,{"disambiguationData":[TD([[makeQuery(id+"F4.imprint","IMPRINT",EDGE,{"derivedFrom":sQuery(id+"F4.wireOp",EDGE,"E58")}),-1.0]])]});
            var Q55;
            Q55=makeQuery(id+"F4.imprint","IMPRINT",FACE,{"disambiguationData":[TD([[makeQuery(id+"F4.imprint","IMPRINT",EDGE,{"derivedFrom":sQuery(id+"F4.wireOp",EDGE,"E78")}),-1.0]])]});
            extrude(context, id + "F5", {"entities" : qUnion([Q0, Q1, Q2, Q3, Q4, Q5, Q6, Q7, Q8, Q9, Q10, Q11, Q12, Q13, Q14, Q15, Q16, Q17, Q18, Q19, Q20, Q21, Q22, Q23, Q24, Q25, Q26, Q27, Q28, Q29, Q30, Q31, Q32, Q33, Q34, Q35, Q36, Q37, Q38, Q39, Q40, Q41, Q42, Q43, Q44, Q45, Q46, Q47, Q48, Q49, Q50, Q51, Q52, Q53, Q54, Q55]), "operationType" : NewBodyOperationType.REMOVE, "oppositeDirection" : true, "depth" : 0.08 * mm, "offsetDistance" : 25.4 * mm});
        }
    });
